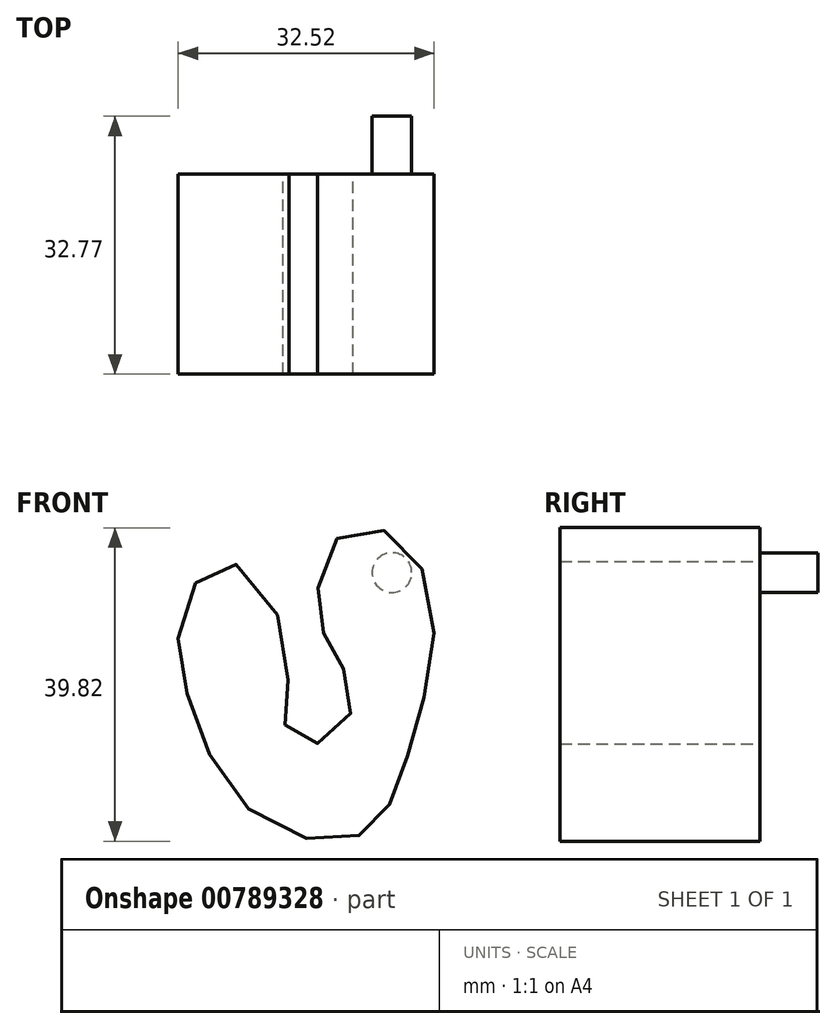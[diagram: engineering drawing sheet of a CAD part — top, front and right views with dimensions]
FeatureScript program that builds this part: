
annotation { "Feature Type Name" : "Feature", "Feature Type Description" : "" }
export const myFeature = defineFeature(function(context is Context, id is Id, definition is map)
    precondition{}
    {
        {
            var Q0;
            Q0=qCreatedBy(makeId("Front.planeOp"),FACE);
            var sketch = newSketch(context, id + "F0", { "sketchPlane" : qUnion([Q0])});
            skFitSpline(sketch, "E0", {"points": [v(0, 0) * mm, v(-7.48, 13.47) * mm, v(-8.57, 24.36) * mm, v(-2.86, 31.43) * mm, v(5.03, 20) * mm, v(4.5, 11.02) * mm, v(8.57, 8.3) * mm, v(13.2, 13.2) * mm, v(10.75, 20) * mm, v(8.84, 24.9) * mm, v(11.02, 34.15) * mm, v(18.64, 34.7) * mm, v(23.54, 23.27) * mm, v(20.82, 9.12) * mm, v(17.55, 0) * mm, v(12.11, -3.95) * mm, v(0, 0) * mm]});
            skSolve(sketch);
        }
        {
            var Q0;
            Q0=makeQuery(id+"F0.imprint","IMPRINT",FACE,{"disambiguationData":[TD([[makeQuery(id+"F0.imprint","IMPRINT",EDGE,{"derivedFrom":sQuery(id+"F0.wireOp",EDGE,"E0")}),-1.0]])]});
            extrude(context, id + "F1", {"entities" : qUnion([Q0]), "depth" : 25.4 * mm, "offsetDistance" : 25.4 * mm});
        }
        {
            var Q0;
            Q0=qCreatedBy(makeId("Front.planeOp"),FACE);
            var sketch = newSketch(context, id + "F2", { "sketchPlane" : qUnion([Q0])});
            skCircle(sketch, "E1", {"center": v(18.18, 30.04) * mm, "radius": 2.52 * mm});
            skSolve(sketch);
        }
        {
            var Q0;
            Q0 = qSketchRegion(id + "F2", true);
            extrude(context, id + "F3", {"entities" : qUnion([Q0]), "operationType" : NewBodyOperationType.ADD, "oppositeDirection" : true, "depth" : 7.37 * mm, "offsetDistance" : 25.4 * mm});
        }
    });
